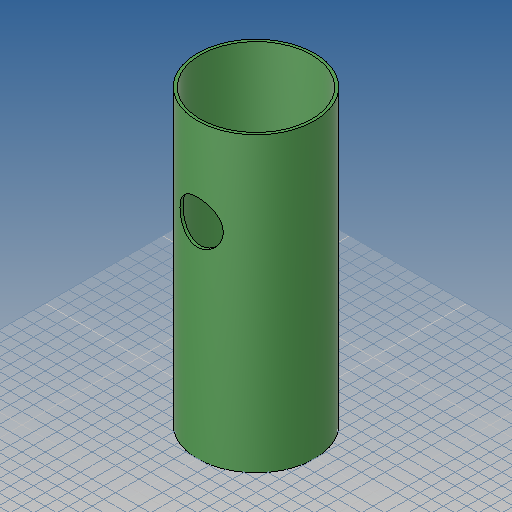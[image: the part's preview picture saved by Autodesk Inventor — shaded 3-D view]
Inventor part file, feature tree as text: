
AUTODESK INVENTOR PART (.ipt)
format: ipt  version: 2019 (Build 230136000, 136)  size: 130,048 bytes
history: native  units: mm
features: extrude x2, sketch x2, other x1
ambient origin geometry x8: Origin, YZ Plane, XZ Plane, XY Plane, X Axis, Y Axis, Z Axis, Center Point
bodies: Volumenkörper1 (feature_tree)
feature tree (5):
  other  "<userpath>\OneDrive\Dokumente\Inventor\Absauganlage\Absauganlage_Params.xlsx"
  extrude  "Extrusion1"  Depth=4.9mm
  extrude  "Extrusion2"  Depth=500.0mm
  sketch  "Skizze1"  dims[d0=200.0mm d1=4.9mm]
  sketch  "Skizze2"  dims[d2=500.0mm d3=0.0mm d4=74.0mm d6=150.0mm d7=500.0mm d8=0.0mm]
